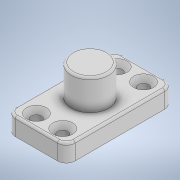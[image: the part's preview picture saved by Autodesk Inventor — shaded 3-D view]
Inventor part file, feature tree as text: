
AUTODESK INVENTOR PART (.ipt)
format: ipt  version: 2020.3 (Build 243373000, 373)  size: 174,592 bytes
history: native  units: mm
features: other x3, sketch x1
ambient origin geometry x8: Origin, YZ Plane, XZ Plane, XY Plane, X Axis, Y Axis, Z Axis, Center Point
bodies: Solid1 (feature_tree)
feature tree (4):
  other  "LegPin_v1.ipt"
  other  "Solid1::LegPin_v1.ipt"
  other  "TaggingFeature1"
  sketch  "Sketch1"  dims[d0=10.0mm]
